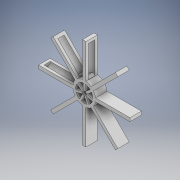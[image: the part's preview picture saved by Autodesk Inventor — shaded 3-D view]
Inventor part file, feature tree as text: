
AUTODESK INVENTOR PART (.ipt)
format: ipt  version: 2020.3 (Build 243373000, 373)  size: 270,336 bytes
history: native  units: mm
features: pattern_circular x2, sketch x2, other x1, extrude x1, revolve x1, fillet x1
ambient origin geometry x8: Origin, YZ Plane, XZ Plane, XY Plane, X Axis, Y Axis, Z Axis, Center Point
bodies: Body1 (feature_tree)
feature tree (8):
  other  "Твердое тело1"
  extrude  "Выдавливание1"  Depth=80.0mm
  revolve  "Вращение1"
  fillet  "Сопряжение1"  Radius=20.0mm
  pattern_circular  "Круговой массив1"  [2 undecoded]
  pattern_circular  "Круговой массив2"  [2 undecoded]
  sketch  "Эскиз1"
  sketch  "Эскиз2"
note: 4 required parameter values undecoded (feature->parameter linkage not recoverable at this tier; creation-order binding heuristic only, values carry confidence <= 0.55)
